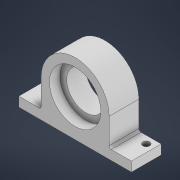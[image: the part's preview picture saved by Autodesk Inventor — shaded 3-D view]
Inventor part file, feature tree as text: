
AUTODESK INVENTOR PART (.ipt)
format: ipt  version: 2021 (Build 250183000, 183)  size: 170,496 bytes
history: native  units: mm
features: extrude x6, sketch x6, fillet x2
ambient origin geometry x8: Origin, YZ Plane, XZ Plane, XY Plane, X Axis, Y Axis, Z Axis, Center Point
bodies: Volumenkörper1 (feature_tree)
feature tree (14):
  extrude  "Extrusion1"  Depth=32.0mm
  sketch  "Skizze2"  dims[d2=24.2mm d3=14.0mm d4=0.0mm]
  extrude  "Extrusion2"  Depth=14.0mm TaperAngle=0.0deg
  extrude  "Extrusion3"  Depth=3.0mm
  extrude  "Extrusion4"  Depth=10.5mm TaperAngle=0.0deg
  fillet  "Rundung1"  Radius=24.2mm
  extrude  "Extrusion5"  Depth=9.0mm TaperAngle=0.0deg
  fillet  "Rundung2"  Radius=16.0mm
  extrude  "Extrusion6"  Depth=1.0mm
  sketch  "Skizze1"  dims[d0=32.0mm d1=32.0mm]
  sketch  "Skizze3"  dims[d5=3.0mm d6=3.0mm]
  sketch  "Skizze4"  dims[d7=10.5mm d8=0.0mm d9=10.5mm d10=0.0mm d11=24.2mm]
  sketch  "Skizze5"  dims[d12=18.0mm d13=9.0mm d14=0.0mm d15=16.0mm]
  sketch  "Skizze6"  dims[d16=3.2mm d17=3.5mm d18=3.5mm d19=3.2mm d20=3.5mm d21=3.5mm d22=5.0mm d23=0.0mm d24=1.0mm d25=3.2mm d26=3.2mm d27=1.5mm d28=0.0mm]
